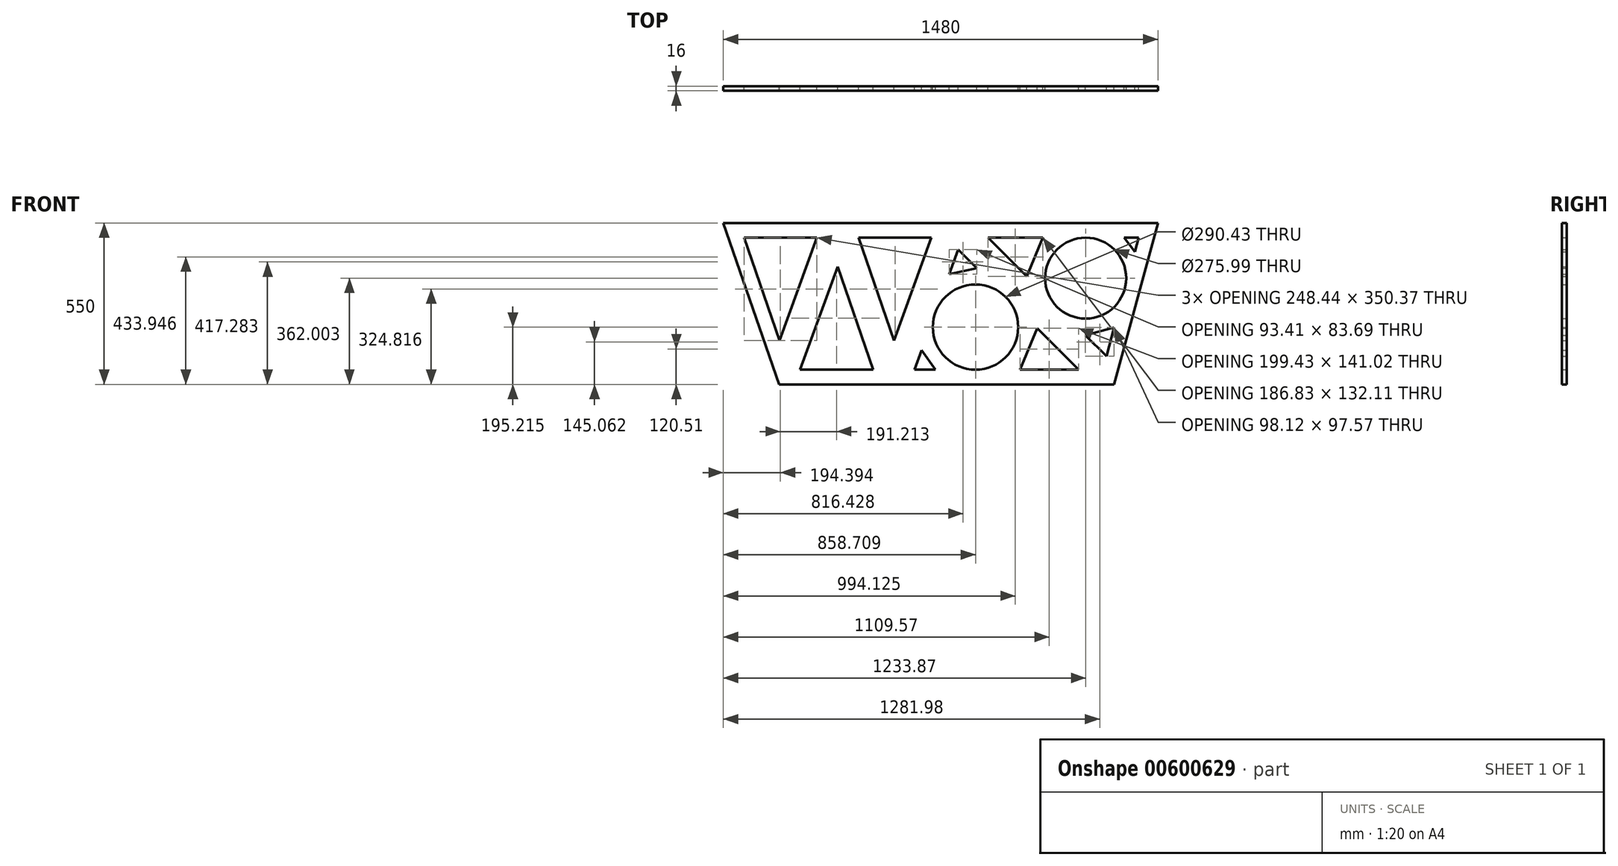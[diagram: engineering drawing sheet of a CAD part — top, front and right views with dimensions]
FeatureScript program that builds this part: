
annotation { "Feature Type Name" : "Feature", "Feature Type Description" : "" }
export const myFeature = defineFeature(function(context is Context, id is Id, definition is map)
    precondition{}
    {
        {
            var Q0;
            Q0=qCreatedBy(makeId("Front.planeOp"),FACE);
            var sketch = newSketch(context, id + "F0", { "sketchPlane" : qUnion([Q0])});
            skPoint(sketch, "E0", {"position": v(0, 0) * mm});
            skPoint(sketch, "E1", {"position": v(0, 550) * mm});
            skPoint(sketch, "E2", {"position": v(-550, 550) * mm});
            skPoint(sketch, "E3", {"position": v(-550, 700) * mm});
            skPoint(sketch, "E4", {"position": v(-750, 0) * mm});
            skPoint(sketch, "E5", {"position": v(-940, 550) * mm});
            skPoint(sketch, "E6", {"position": v(-940, 750) * mm});
            skPoint(sketch, "E7", {"position": v(-1330, 550) * mm});
            skPoint(sketch, "E8", {"position": v(-1140, 0) * mm});
            skPoint(sketch, "E9", {"position": v(-1330, 850) * mm});
            skPoint(sketch, "E10", {"position": v(150, 550) * mm});
            skLineSegment(sketch, "E11", {"start": v(0, 0) * mm, "end": v(150, 550) * mm});
            skLineSegment(sketch, "E12", {"start": v(150, 550) * mm, "end": v(-550, 550) * mm});
            skLineSegment(sketch, "E13", {"start": v(-940, 550) * mm, "end": v(-550, 550) * mm});
            skLineSegment(sketch, "E14", {"start": v(-940, 550) * mm, "end": v(-1330, 550) * mm});
            skLineSegment(sketch, "E15", {"start": v(-750, 0) * mm, "end": v(0, 0) * mm});
            skLineSegment(sketch, "E16", {"start": v(-1330, 550) * mm, "end": v(-1330, 850) * mm});
            skLineSegment(sketch, "E17", {"start": v(-940, 550) * mm, "end": v(-940, 750) * mm});
            skLineSegment(sketch, "E18", {"start": v(-550, 700) * mm, "end": v(-550, 550) * mm});
            skLineSegment(sketch, "E19.0", {"start": v(-1011.38, 500) * mm, "end": v(-1138.8, 149.63) * mm});
            skLineSegment(sketch, "E19.1", {"start": v(-1011.38, 500) * mm, "end": v(-1259.83, 500) * mm});
            skLineSegment(sketch, "E19.2", {"start": v(-1138.8, 149.63) * mm, "end": v(-1259.83, 500) * mm});
            skLineSegment(sketch, "E20.0", {"start": v(-941.2, 400.37) * mm, "end": v(-1068.62, 50) * mm});
            skLineSegment(sketch, "E20.1", {"start": v(-820.17, 50) * mm, "end": v(-941.2, 400.37) * mm});
            skLineSegment(sketch, "E20.2", {"start": v(-820.17, 50) * mm, "end": v(-1068.62, 50) * mm});
            skLineSegment(sketch, "E21.0", {"start": v(-748.8, 149.63) * mm, "end": v(-869.83, 500) * mm});
            skLineSegment(sketch, "E21.1", {"start": v(-621.38, 500) * mm, "end": v(-748.8, 149.63) * mm});
            skLineSegment(sketch, "E21.2", {"start": v(-869.83, 500) * mm, "end": v(-621.38, 500) * mm});
            skCircle(sketch, "E22", {"center": v(-471.3, 195.22) * mm, "radius": 145.22 * mm});
            skCircle(sketch, "E23", {"center": v(-96.14, 362) * mm, "radius": 138 * mm});
            skLineSegment(sketch, "E24", {"start": v(-223.63, 414.81) * mm, "end": v(-269.82, 433.95) * mm});
            skLineSegment(sketch, "E25", {"start": v(13.53, 445.77) * mm, "end": v(53.27, 476.12) * mm});
            skLineSegment(sketch, "E26", {"start": v(-60.85, 229.14) * mm, "end": v(-48.02, 180.82) * mm});
            skLineSegment(sketch, "E27", {"start": v(-269.82, 433.95) * mm, "end": v(-242.46, 500) * mm});
            skLineSegment(sketch, "E28", {"start": v(-269.82, 433.95) * mm, "end": v(-297.18, 367.9) * mm});
            skLineSegment(sketch, "E29", {"start": v(53.27, 476.12) * mm, "end": v(35.02, 500) * mm});
            skLineSegment(sketch, "E30", {"start": v(53.27, 476.12) * mm, "end": v(71.5, 452.23) * mm});
            skLineSegment(sketch, "E31", {"start": v(-48.02, 180.82) * mm, "end": v(1.04, 193.84) * mm});
            skLineSegment(sketch, "E32", {"start": v(1.04, 193.84) * mm, "end": v(-48.02, 180.82) * mm});
            skLineSegment(sketch, "E33", {"start": v(-48.02, 180.82) * mm, "end": v(-97.08, 167.79) * mm});
            skLineSegment(sketch, "E34", {"start": v(-502.74, 336.98) * mm, "end": v(-513.57, 385.8) * mm});
            skLineSegment(sketch, "E35", {"start": v(-337.13, 139.64) * mm, "end": v(-290.94, 120.5) * mm});
            skLineSegment(sketch, "E36", {"start": v(-590.23, 111.9) * mm, "end": v(-631.19, 83.22) * mm});
            skLineSegment(sketch, "E37", {"start": v(-513.57, 385.8) * mm, "end": v(-466.87, 396.16) * mm});
            skLineSegment(sketch, "E38", {"start": v(-466.87, 396.16) * mm, "end": v(-513.57, 385.8) * mm});
            skLineSegment(sketch, "E39", {"start": v(-513.57, 385.8) * mm, "end": v(-560.27, 375.44) * mm});
            skLineSegment(sketch, "E40", {"start": v(-290.94, 120.5) * mm, "end": v(-261.73, 191.02) * mm});
            skLineSegment(sketch, "E41", {"start": v(-261.73, 191.02) * mm, "end": v(-290.94, 120.5) * mm});
            skLineSegment(sketch, "E42", {"start": v(-290.94, 120.5) * mm, "end": v(-320.14, 50) * mm});
            skLineSegment(sketch, "E43", {"start": v(-631.19, 83.22) * mm, "end": v(-654.45, 116.44) * mm});
            skLineSegment(sketch, "E44", {"start": v(-654.45, 116.44) * mm, "end": v(-631.19, 83.22) * mm});
            skLineSegment(sketch, "E45", {"start": v(-631.19, 83.22) * mm, "end": v(-607.92, 50) * mm});
            skLineSegment(sketch, "E46", {"start": v(-654.45, 116.44) * mm, "end": v(-678.62, 50) * mm});
            skLineSegment(sketch, "E47", {"start": v(-607.92, 50) * mm, "end": v(-678.62, 50) * mm});
            skLineSegment(sketch, "E48", {"start": v(-320.14, 50) * mm, "end": v(-243.27, 50) * mm});
            skLineSegment(sketch, "E49", {"start": v(-466.87, 396.16) * mm, "end": v(-529.84, 459.13) * mm});
            skLineSegment(sketch, "E50", {"start": v(-560.27, 375.44) * mm, "end": v(-529.84, 459.13) * mm});
            skLineSegment(sketch, "E51", {"start": v(-261.73, 191.02) * mm, "end": v(-120.71, 50) * mm});
            skLineSegment(sketch, "E52", {"start": v(-120.71, 50) * mm, "end": v(-320.14, 50) * mm});
            skLineSegment(sketch, "E53", {"start": v(-242.46, 500) * mm, "end": v(-429.29, 500) * mm});
            skLineSegment(sketch, "E54", {"start": v(-297.18, 367.9) * mm, "end": v(-429.29, 500) * mm});
            skLineSegment(sketch, "E55", {"start": v(35.02, 500) * mm, "end": v(84.54, 500) * mm});
            skLineSegment(sketch, "E56", {"start": v(71.5, 452.23) * mm, "end": v(84.54, 500) * mm});
            skLineSegment(sketch, "E57", {"start": v(1.04, 193.84) * mm, "end": v(-25.57, 96.28) * mm});
            skLineSegment(sketch, "E58", {"start": v(-97.08, 167.79) * mm, "end": v(-25.57, 96.28) * mm});
            skLineSegment(sketch, "E59", {"start": v(-429.29, 500) * mm, "end": v(-297.18, 367.9) * mm});
            skLineSegment(sketch, "E60", {"start": v(-1330, 550) * mm, "end": v(-1140, 0) * mm});
            skLineSegment(sketch, "E61", {"start": v(-750, 0) * mm, "end": v(-1140, 0) * mm});
            skSolve(sketch);
        }
        {
            var Q0;
            {var subQ5=sQuery(id+"F0.wireOp",EDGE,"E11");Q0=makeQuery(id+"F0.imprint","IMPRINT",FACE,{"disambiguationData":[TD([[makeQuery(id+"F0.imprint","IMPRINT",EDGE,{"derivedFrom":subQ5}),1.0]])]});}
            extrude(context, id + "F1", {"entities" : qUnion([Q0]), "depth" : 16 * mm, "offsetDistance" : 25 * mm});
        }
    });
